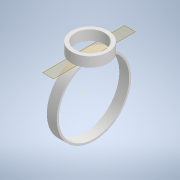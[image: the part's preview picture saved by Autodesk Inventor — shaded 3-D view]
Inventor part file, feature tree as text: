
AUTODESK INVENTOR PART (.ipt)
format: ipt  version: 2021 (Build 250183000, 183)  size: 120,320 bytes
history: native  units: mm
features: sketch x4, extrude x2, plane x1
ambient origin geometry x8: Origin, YZ Plane, XZ Plane, XY Plane, X Axis, Y Axis, Z Axis, Center Point
bodies: Solid1 (feature_tree)
feature tree (7):
  extrude  "Extrusion1"  Depth=71.0mm
  sketch  "Sketch2"  dims[d2=10.0mm d3=0.0mm d6=37.0mm]
  plane  "Work Plane1"
  sketch  "Sketch3"  dims[d7=29.625mm]
  extrude  "Extrusion2"  Depth=10.0mm
  sketch  "Sketch1"  dims[d0=75.0mm d1=71.0mm]
  sketch  "Sketch4"  dims[d8=10.0mm d9=0.0mm]
